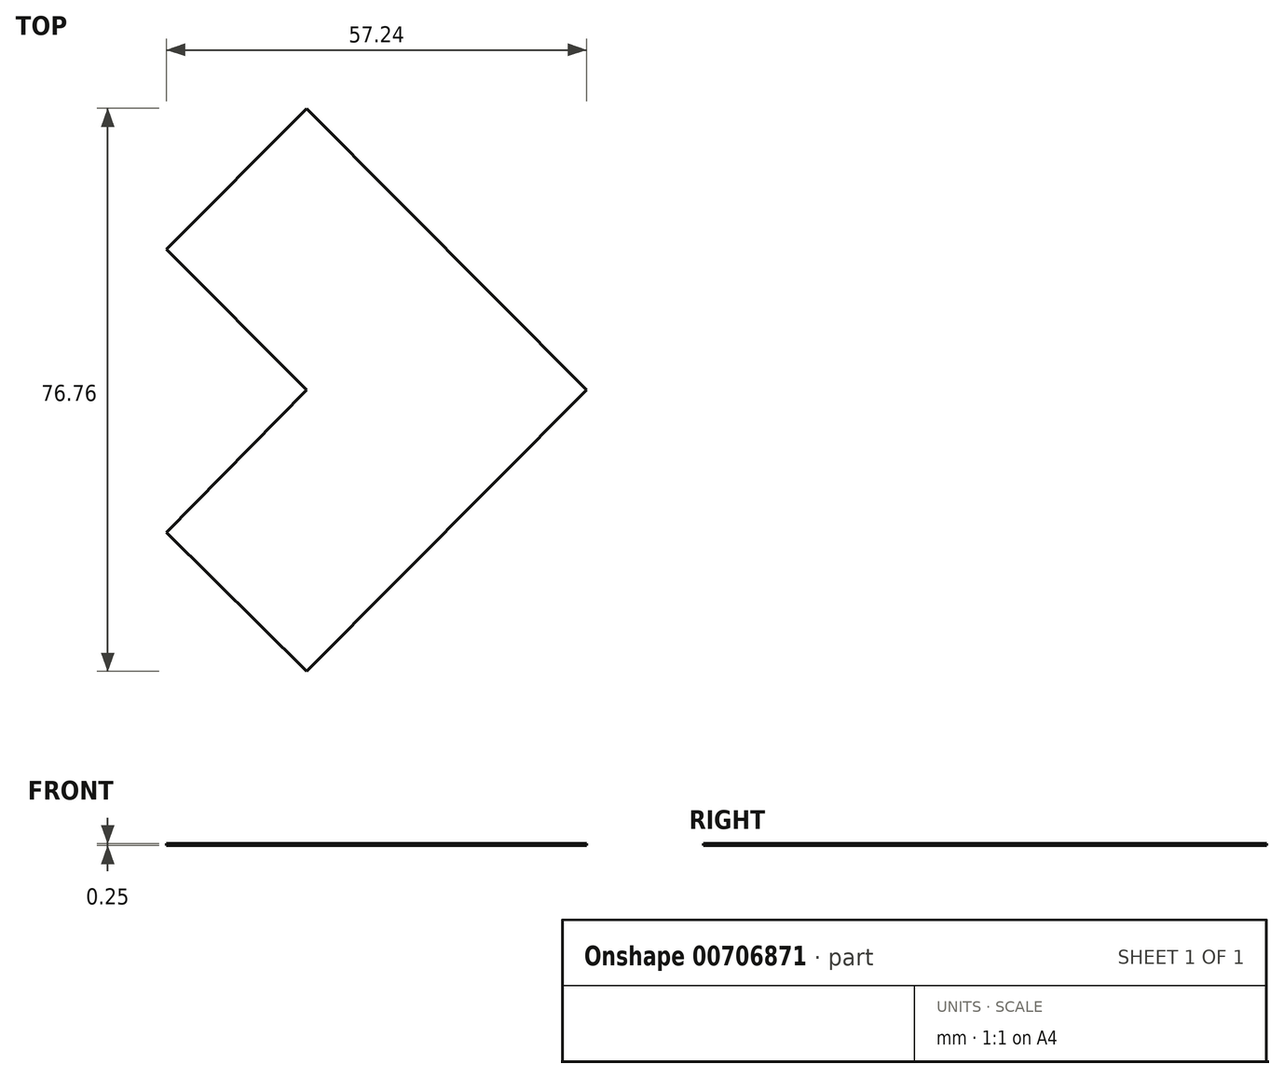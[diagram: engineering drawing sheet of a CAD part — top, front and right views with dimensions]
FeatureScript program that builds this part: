
annotation { "Feature Type Name" : "Feature", "Feature Type Description" : "" }
export const myFeature = defineFeature(function(context is Context, id is Id, definition is map)
    precondition{}
    {
        {
            var Q0;
            Q0=qCreatedBy(makeId("Top.planeOp"),FACE);
            var sketch = newSketch(context, id + "F0", { "sketchPlane" : qUnion([Q0])});
            skLineSegment(sketch, "E0", {"start": v(-6.27, -8.78) * mm, "end": v(-44.43, 29.6) * mm});
            skLineSegment(sketch, "E1", {"start": v(-6.27, -8.78) * mm, "end": v(-44.43, -47.16) * mm});
            skLineSegment(sketch, "E2", {"start": v(-44.43, -47.16) * mm, "end": v(-63.51, -28.2) * mm});
            skLineSegment(sketch, "E3", {"start": v(-63.51, -28.2) * mm, "end": v(-44.43, -8.78) * mm});
            skLineSegment(sketch, "E4", {"start": v(-44.43, -8.78) * mm, "end": v(-63.51, 10.4) * mm});
            skLineSegment(sketch, "E5", {"start": v(-63.51, 10.4) * mm, "end": v(-44.43, 29.6) * mm});
            skSolve(sketch);
        }
        {
            var Q0;
            Q0 = qSketchRegion(id + "F0", true);
            extrude(context, id + "F1", {"entities" : qUnion([Q0]), "depth" : 0.25 * mm, "offsetDistance" : 25.4 * mm});
        }
    });
